# Revit family: FOR update 72530USA_new
name_source: partatom
category: Plumbing Fixtures
revit_build: Autodesk Revit 2018 (Build: 20170223_1515(x64)
units: mm (PartAtom-declared; Revit-internal decimal feet)

## family parameters
Always vertical = No
Cut with Voids When Loaded = No
OmniClass Number = 23.45.55.17
OmniClass Title = Mixing Faucets
Part Type = Normal
Room Calculation Point = No
Round Connector Dimension = Use Diameter
Shared = No
Work Plane-Based = Yes

## types (3) — shared parameters
Always visible = Yes
BIMobject category = Taps & Mixers
Cold Water Inlet = 10 mm
Cold Water Inlet Description = Cold Water Inlet 9.5mm
Default Elevation = 1219.2 mm  [stored 4 ft]
Description = Rebris S 3-hole basin mixer 110 with pop-up waste set
Design country = Germany
EAN code = 4059625420225
Edition number = 1
Hot Water Inlet = 10 mm
Hot Water Inlet Description = Hot Water Inlet 9.5mm
IFC Classification = Valve
Manufacturer = Hansgrohe
Manufacturer country = Germany
Manufacturer name = hansgrohe
Model = 72530USA
OmniClass Code = 23-31 11 00
OmniClass Description = Faucets
Product Guid = 7ca38b32-c6e4-4b8d-bba5-eaf77e4cfb83
Product SKU = 72530USA
Product data url = https://bimobject.com
Product family = Rebris S
Product group = Basin mixers
Product name = 72530USA Rebris S 3-hole basin mixer 110 with pop-up waste set
QR code = https://bimobject.com
UNSPSC Code = 301815
URL = https://www.hansgrohe.com
Weight Net (Kg) = 3

## per-type parameters (varying)
| type | Material 1 |
| 671 Matte Black | Hansgrohe - Metal - 671 Matte Black |
| 001 Chrome | Hansgrohe - Metal - 001 Chrome |
| 821 Brushed Nickel | Hansgrohe - Metal - 821 Brushed Nickel |

note: [stored X ft] marks values corroborated as IEEE doubles in the binary element streams (Revit-internal decimal feet)

## geometry (parser evidence)
native form markers: Sweep x2
no freeform markers — native parametric forms only
